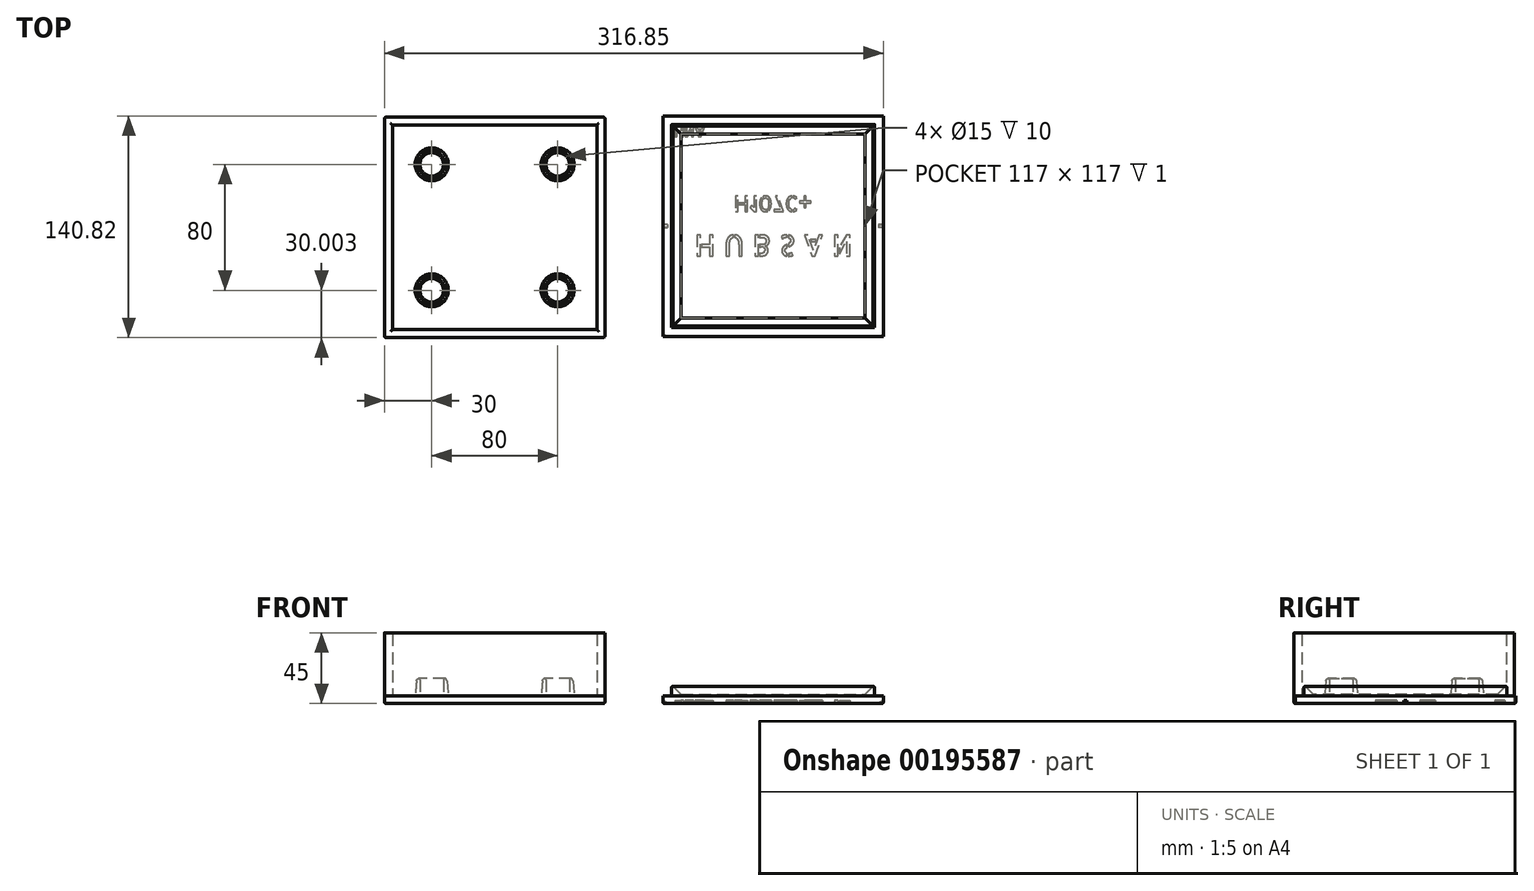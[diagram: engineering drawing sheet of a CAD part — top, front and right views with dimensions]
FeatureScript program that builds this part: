
annotation { "Feature Type Name" : "Feature", "Feature Type Description" : "" }
export const myFeature = defineFeature(function(context is Context, id is Id, definition is map)
    precondition{}
    {
        {
            var Q0;
            Q0=qCreatedBy(makeId("Top.planeOp"),FACE);
            var sketch = newSketch(context, id + "F0", { "sketchPlane" : qUnion([Q0])});
            skLineSegment(sketch, "E0.bottom", {"start": v(65, -65.82) * mm, "end": v(-65, -65.82) * mm});
            skLineSegment(sketch, "E0.top", {"start": v(65, 64.18) * mm, "end": v(-65, 64.18) * mm});
            skLineSegment(sketch, "E0.left", {"start": v(65, -65.82) * mm, "end": v(65, 64.18) * mm});
            skLineSegment(sketch, "E0.right", {"start": v(-65, -65.82) * mm, "end": v(-65, 64.18) * mm});
            skPoint(sketch, "E0.middle", {"position": v(0, -0.82) * mm});
            skLineSegment(sketch, "E1.0", {"start": v(70, 69.18) * mm, "end": v(-70, 69.18) * mm});
            skLineSegment(sketch, "E1.1", {"start": v(70, -70.82) * mm, "end": v(70, 69.18) * mm});
            skLineSegment(sketch, "E1.2", {"start": v(70, -70.82) * mm, "end": v(-70, -70.82) * mm});
            skLineSegment(sketch, "E1.3", {"start": v(-70, -70.82) * mm, "end": v(-70, 69.18) * mm});
            skCircle(sketch, "E2", {"center": v(-40, 39.18) * mm, "radius": 7.5 * mm});
            skCircle(sketch, "E3.0", {"center": v(-40, 39.18) * mm, "radius": 10.5 * mm});
            skCircle(sketch, "E4", {"center": v(-40, -40.82) * mm, "radius": 7.5 * mm});
            skCircle(sketch, "E5.0", {"center": v(-40, -40.82) * mm, "radius": 10.5 * mm});
            skCircle(sketch, "E6", {"center": v(40, -40.82) * mm, "radius": 7.5 * mm});
            skCircle(sketch, "E7.0", {"center": v(40, -40.82) * mm, "radius": 10.5 * mm});
            skCircle(sketch, "E8", {"center": v(40, 39.18) * mm, "radius": 7.5 * mm});
            skCircle(sketch, "E9.0", {"center": v(40, 39.18) * mm, "radius": 10.5 * mm});
            skSolve(sketch);
        }
        {
            var Q0;
            Q0=makeQuery(id+"F0.imprint","IMPRINT",FACE,{"disambiguationData":[TD([[makeQuery(id+"F0.imprint","IMPRINT",EDGE,{"derivedFrom":sQuery(id+"F0.wireOp",EDGE,"E2")}),-1.0]])]});
            var Q1;
            Q1=makeQuery(id+"F0.imprint","IMPRINT",FACE,{"disambiguationData":[TD([[makeQuery(id+"F0.imprint","IMPRINT",EDGE,{"derivedFrom":sQuery(id+"F0.wireOp",EDGE,"E8")}),-1.0]])]});
            var Q2;
            Q2=makeQuery(id+"F0.imprint","IMPRINT",FACE,{"disambiguationData":[TD([[makeQuery(id+"F0.imprint","IMPRINT",EDGE,{"derivedFrom":sQuery(id+"F0.wireOp",EDGE,"E6")}),-1.0]])]});
            var Q3;
            Q3=makeQuery(id+"F0.imprint","IMPRINT",FACE,{"disambiguationData":[TD([[makeQuery(id+"F0.imprint","IMPRINT",EDGE,{"derivedFrom":sQuery(id+"F0.wireOp",EDGE,"E4")}),-1.0]])]});
            extrude(context, id + "F1", {"entities" : qUnion([Q0, Q1, Q2, Q3]), "depth" : 11 * mm});
        }
        {
            var Q0;
            Q0=makeQuery(id+"F1.opExtrude","CAP_EDGE",EDGE,{"disambiguationData":[OSD([sQuery(id+"F0.wireOp",EDGE,"E5.0")])],"isStart":false});
            var Q1;
            Q1=makeQuery(id+"F1.opExtrude","CAP_EDGE",EDGE,{"disambiguationData":[OSD([sQuery(id+"F0.wireOp",EDGE,"E3.0")])],"isStart":false});
            var Q2;
            Q2=makeQuery(id+"F1.opExtrude","CAP_EDGE",EDGE,{"disambiguationData":[OSD([sQuery(id+"F0.wireOp",EDGE,"E7.0")])],"isStart":false});
            var Q3;
            Q3=makeQuery(id+"F1.opExtrude","CAP_EDGE",EDGE,{"disambiguationData":[OSD([sQuery(id+"F0.wireOp",EDGE,"E9.0")])],"isStart":false});
            chamfer(context, id + "F2", {"entities" : qUnion([Q0, Q1, Q2, Q3]), "chamferType" : ChamferType.OFFSET_ANGLE, "width" : 1 * mm, "oppositeDirection" : false, "angle" : 85 * degree, "tangentPropagation" : true});
        }
        {
            var Q0;
            Q0=makeQuery(id+"F1.opExtrude","CAP_EDGE",EDGE,{"disambiguationData":[OSD([sQuery(id+"F0.wireOp",EDGE,"E2")])],"isStart":false});
            var Q1;
            Q1=makeQuery(id+"F1.opExtrude","CAP_EDGE",EDGE,{"disambiguationData":[OSD([sQuery(id+"F0.wireOp",EDGE,"E4")])],"isStart":false});
            var Q2;
            Q2=makeQuery(id+"F1.opExtrude","CAP_EDGE",EDGE,{"disambiguationData":[OSD([sQuery(id+"F0.wireOp",EDGE,"E6")])],"isStart":false});
            var Q3;
            Q3=makeQuery(id+"F1.opExtrude","CAP_EDGE",EDGE,{"disambiguationData":[OSD([sQuery(id+"F0.wireOp",EDGE,"E8")])],"isStart":false});
            fillet(context, id + "F3", {"entities" : qUnion([Q0, Q1, Q2, Q3]), "radius" : 1 * mm, "tangentPropagation" : true, "allowEdgeOverflow" : false});
        }
        {
            var Q0;
            {var subQ0=sQuery(id+"F0.wireOp",EDGE,"E3.0");Q0=makeQuery(id+"F2.opChamfer","BLEND_EDGE",EDGE,{"blendedFrom":[makeQuery(id+"F1.opExtrude","CAP_EDGE",EDGE,{"disambiguationData":[OSD([subQ0])],"isStart":false}),makeQuery(id+"F1.opExtrude","CAP_FACE",FACE,{"disambiguationData":[OSD([sQuery(id+"F0.wireOp",EDGE,"E2"),subQ0])],"isStart":false})],"blendedInto":[makeQuery(id+"F1.opExtrude","CAP_FACE",FACE,{"disambiguationData":[OSD([sQuery(id+"F0.wireOp",EDGE,"E2"),subQ0])],"isStart":false})]});}
            var Q1;
            {var subQ0=sQuery(id+"F0.wireOp",EDGE,"E5.0");Q1=makeQuery(id+"F2.opChamfer","BLEND_EDGE",EDGE,{"blendedFrom":[makeQuery(id+"F1.opExtrude","CAP_EDGE",EDGE,{"disambiguationData":[OSD([subQ0])],"isStart":false}),makeQuery(id+"F1.opExtrude","CAP_FACE",FACE,{"disambiguationData":[OSD([sQuery(id+"F0.wireOp",EDGE,"E4"),subQ0])],"isStart":false})],"blendedInto":[makeQuery(id+"F1.opExtrude","CAP_FACE",FACE,{"disambiguationData":[OSD([sQuery(id+"F0.wireOp",EDGE,"E4"),subQ0])],"isStart":false})]});}
            var Q2;
            {var subQ0=sQuery(id+"F0.wireOp",EDGE,"E7.0");Q2=makeQuery(id+"F2.opChamfer","BLEND_EDGE",EDGE,{"blendedFrom":[makeQuery(id+"F1.opExtrude","CAP_EDGE",EDGE,{"disambiguationData":[OSD([subQ0])],"isStart":false}),makeQuery(id+"F1.opExtrude","CAP_FACE",FACE,{"disambiguationData":[OSD([sQuery(id+"F0.wireOp",EDGE,"E6"),subQ0])],"isStart":false})],"blendedInto":[makeQuery(id+"F1.opExtrude","CAP_FACE",FACE,{"disambiguationData":[OSD([sQuery(id+"F0.wireOp",EDGE,"E6"),subQ0])],"isStart":false})]});}
            var Q3;
            {var subQ0=sQuery(id+"F0.wireOp",EDGE,"E9.0");Q3=makeQuery(id+"F2.opChamfer","BLEND_EDGE",EDGE,{"blendedFrom":[makeQuery(id+"F1.opExtrude","CAP_EDGE",EDGE,{"disambiguationData":[OSD([subQ0])],"isStart":false}),makeQuery(id+"F1.opExtrude","CAP_FACE",FACE,{"disambiguationData":[OSD([sQuery(id+"F0.wireOp",EDGE,"E8"),subQ0])],"isStart":false})],"blendedInto":[makeQuery(id+"F1.opExtrude","CAP_FACE",FACE,{"disambiguationData":[OSD([sQuery(id+"F0.wireOp",EDGE,"E8"),subQ0])],"isStart":false})]});}
            fillet(context, id + "F4", {"entities" : qUnion([Q0, Q1, Q2, Q3]), "radius" : 2 * mm, "tangentPropagation" : true, "allowEdgeOverflow" : false});
        }
        {
            var Q0;
            Q0=makeQuery(id+"F0.imprint","IMPRINT",FACE,{"disambiguationData":[TD([[makeQuery(id+"F0.imprint","IMPRINT",EDGE,{"derivedFrom":sQuery(id+"F0.wireOp",EDGE,"E0.bottom")}),1.0]])]});
            extrude(context, id + "F5", {"entities" : qUnion([Q0]), "depth" : 40 * mm});
        }
        {
            var Q0;
            Q0=makeQuery(id+"F0.imprint","IMPRINT",FACE,{"disambiguationData":[TD([[makeQuery(id+"F0.imprint","IMPRINT",EDGE,{"derivedFrom":sQuery(id+"F0.wireOp",EDGE,"E0.bottom")}),-1.0]])]});
            var Q1;
            Q1=makeQuery(id+"F0.imprint","IMPRINT",FACE,{"disambiguationData":[TD([[makeQuery(id+"F0.imprint","IMPRINT",EDGE,{"derivedFrom":sQuery(id+"F0.wireOp",EDGE,"E0.bottom")}),1.0]])]});
            var Q2;
            Q2=makeQuery(id+"F0.imprint","IMPRINT",FACE,{"disambiguationData":[TD([[makeQuery(id+"F0.imprint","IMPRINT",EDGE,{"derivedFrom":sQuery(id+"F0.wireOp",EDGE,"E4")}),1.0]])]});
            var Q3;
            Q3=makeQuery(id+"F0.imprint","IMPRINT",FACE,{"disambiguationData":[TD([[makeQuery(id+"F0.imprint","IMPRINT",EDGE,{"derivedFrom":sQuery(id+"F0.wireOp",EDGE,"E4")}),-1.0]])]});
            var Q4;
            Q4=makeQuery(id+"F0.imprint","IMPRINT",FACE,{"disambiguationData":[TD([[makeQuery(id+"F0.imprint","IMPRINT",EDGE,{"derivedFrom":sQuery(id+"F0.wireOp",EDGE,"E2")}),-1.0]])]});
            var Q5;
            Q5=makeQuery(id+"F0.imprint","IMPRINT",FACE,{"disambiguationData":[TD([[makeQuery(id+"F0.imprint","IMPRINT",EDGE,{"derivedFrom":sQuery(id+"F0.wireOp",EDGE,"E2")}),1.0]])]});
            var Q6;
            Q6=makeQuery(id+"F0.imprint","IMPRINT",FACE,{"disambiguationData":[TD([[makeQuery(id+"F0.imprint","IMPRINT",EDGE,{"derivedFrom":sQuery(id+"F0.wireOp",EDGE,"E6")}),-1.0]])]});
            var Q7;
            Q7=makeQuery(id+"F0.imprint","IMPRINT",FACE,{"disambiguationData":[TD([[makeQuery(id+"F0.imprint","IMPRINT",EDGE,{"derivedFrom":sQuery(id+"F0.wireOp",EDGE,"E6")}),1.0]])]});
            var Q8;
            Q8=makeQuery(id+"F0.imprint","IMPRINT",FACE,{"disambiguationData":[TD([[makeQuery(id+"F0.imprint","IMPRINT",EDGE,{"derivedFrom":sQuery(id+"F0.wireOp",EDGE,"E8")}),-1.0]])]});
            var Q9;
            Q9=makeQuery(id+"F0.imprint","IMPRINT",FACE,{"disambiguationData":[TD([[makeQuery(id+"F0.imprint","IMPRINT",EDGE,{"derivedFrom":sQuery(id+"F0.wireOp",EDGE,"E8")}),1.0]])]});
            extrude(context, id + "F6", {"entities" : qUnion([Q0, Q1, Q2, Q3, Q4, Q5, Q6, Q7, Q8, Q9]), "oppositeDirection" : true, "depth" : 5 * mm});
        }
        {
            var Q0;
            Q0=makeQuery(id+"F6.opExtrude","CAP_EDGE",EDGE,{"disambiguationData":[OSD([sQuery(id+"F0.wireOp",EDGE,"E1.2")])],"isStart":false});
            var Q1;
            Q1=makeQuery(id+"F6.opExtrude","CAP_EDGE",EDGE,{"disambiguationData":[OSD([sQuery(id+"F0.wireOp",EDGE,"E1.3")])],"isStart":false});
            var Q2;
            Q2=makeQuery(id+"F6.opExtrude","CAP_EDGE",EDGE,{"disambiguationData":[OSD([sQuery(id+"F0.wireOp",EDGE,"E1.1")])],"isStart":false});
            var Q3;
            Q3=makeQuery(id+"F6.opExtrude","CAP_EDGE",EDGE,{"disambiguationData":[OSD([sQuery(id+"F0.wireOp",EDGE,"E1.0")])],"isStart":false});
            var Q4;
            Q4=makeQuery(id+"F6.opExtrude","SWEPT_EDGE",EDGE,{"disambiguationData":[OSD([sQuery(id+"F0.wireOp",EDGE,"E1.2"),sQuery(id+"F0.wireOp",EDGE,"E1.3")])]});
            var Q5;
            Q5=makeQuery(id+"F5.opExtrude","SWEPT_EDGE",EDGE,{"disambiguationData":[OSD([sQuery(id+"F0.wireOp",EDGE,"E1.2"),sQuery(id+"F0.wireOp",EDGE,"E1.3")])]});
            var Q6;
            Q6=makeQuery(id+"F5.opExtrude","SWEPT_EDGE",EDGE,{"disambiguationData":[OSD([sQuery(id+"F0.wireOp",EDGE,"E1.1"),sQuery(id+"F0.wireOp",EDGE,"E1.2")])]});
            var Q7;
            Q7=makeQuery(id+"F6.opExtrude","SWEPT_EDGE",EDGE,{"disambiguationData":[OSD([sQuery(id+"F0.wireOp",EDGE,"E1.1"),sQuery(id+"F0.wireOp",EDGE,"E1.2")])]});
            var Q8;
            Q8=makeQuery(id+"F6.opExtrude","SWEPT_EDGE",EDGE,{"disambiguationData":[OSD([sQuery(id+"F0.wireOp",EDGE,"E1.0"),sQuery(id+"F0.wireOp",EDGE,"E1.1")])]});
            var Q9;
            Q9=makeQuery(id+"F5.opExtrude","SWEPT_EDGE",EDGE,{"disambiguationData":[OSD([sQuery(id+"F0.wireOp",EDGE,"E1.0"),sQuery(id+"F0.wireOp",EDGE,"E1.1")])]});
            var Q10;
            Q10=makeQuery(id+"F6.opExtrude","SWEPT_EDGE",EDGE,{"disambiguationData":[OSD([sQuery(id+"F0.wireOp",EDGE,"E1.0"),sQuery(id+"F0.wireOp",EDGE,"E1.3")])]});
            var Q11;
            Q11=makeQuery(id+"F5.opExtrude","SWEPT_EDGE",EDGE,{"disambiguationData":[OSD([sQuery(id+"F0.wireOp",EDGE,"E1.0"),sQuery(id+"F0.wireOp",EDGE,"E1.3")])]});
            var Q12;
            Q12=makeQuery(id+"F5.opExtrude","CAP_EDGE",EDGE,{"disambiguationData":[OSD([sQuery(id+"F0.wireOp",EDGE,"E0.right")])],"isStart":false});
            var Q13;
            Q13=makeQuery(id+"F5.opExtrude","CAP_EDGE",EDGE,{"disambiguationData":[OSD([sQuery(id+"F0.wireOp",EDGE,"E0.bottom")])],"isStart":false});
            var Q14;
            Q14=makeQuery(id+"F5.opExtrude","CAP_EDGE",EDGE,{"disambiguationData":[OSD([sQuery(id+"F0.wireOp",EDGE,"E0.left")])],"isStart":false});
            var Q15;
            Q15=makeQuery(id+"F5.opExtrude","CAP_EDGE",EDGE,{"disambiguationData":[OSD([sQuery(id+"F0.wireOp",EDGE,"E0.top")])],"isStart":false});
            fillet(context, id + "F7", {"entities" : qUnion([Q0, Q1, Q2, Q3, Q4, Q5, Q6, Q7, Q8, Q9, Q10, Q11, Q12, Q13, Q14, Q15]), "radius" : 1 * mm, "tangentPropagation" : true, "allowEdgeOverflow" : false});
        }
        {
            var Q0;
            Q0=qCreatedBy(makeId("Top.planeOp"),FACE);
            var sketch = newSketch(context, id + "F8", { "sketchPlane" : qUnion([Q0])});
            skLineSegment(sketch, "E10.bottom", {"start": v(241.35, -64.5) * mm, "end": v(112.35, -64.5) * mm});
            skLineSegment(sketch, "E10.top", {"start": v(241.35, 64.5) * mm, "end": v(112.35, 64.5) * mm});
            skLineSegment(sketch, "E10.left", {"start": v(241.35, -64.5) * mm, "end": v(241.35, 64.5) * mm});
            skLineSegment(sketch, "E10.right", {"start": v(112.35, -64.5) * mm, "end": v(112.35, 64.5) * mm});
            skPoint(sketch, "E10.middle", {"position": v(176.85, 0) * mm});
            skLineSegment(sketch, "E11.0", {"start": v(106.85, -70) * mm, "end": v(106.85, 70) * mm});
            skLineSegment(sketch, "E11.1", {"start": v(246.85, -70) * mm, "end": v(106.85, -70) * mm});
            skLineSegment(sketch, "E11.2", {"start": v(246.85, -70) * mm, "end": v(246.85, 70) * mm});
            skLineSegment(sketch, "E11.3", {"start": v(246.85, 70) * mm, "end": v(106.85, 70) * mm});
            skLineSegment(sketch, "E12.0", {"start": v(118.35, -58.5) * mm, "end": v(118.35, 58.5) * mm});
            skLineSegment(sketch, "E12.1", {"start": v(235.35, -58.5) * mm, "end": v(118.35, -58.5) * mm});
            skLineSegment(sketch, "E12.2", {"start": v(235.35, -58.5) * mm, "end": v(235.35, 58.5) * mm});
            skLineSegment(sketch, "E12.3", {"start": v(235.35, 58.5) * mm, "end": v(118.35, 58.5) * mm});
            skLineSegment(sketch, "E13", {"start": v(106.85, 0) * mm, "end": v(246.85, 0) * mm, "construction": true});
            skLineSegment(sketch, "E14", {"start": v(176.85, -70) * mm, "end": v(176.85, 70) * mm, "construction": true});
            skSolve(sketch);
        }
        {
            var Q0;
            Q0=makeQuery(id+"F8.imprint","IMPRINT",FACE,{"disambiguationData":[TD([[makeQuery(id+"F8.imprint","IMPRINT",EDGE,{"derivedFrom":sQuery(id+"F8.wireOp",EDGE,"E10.bottom")}),-1.0]])]});
            extrude(context, id + "F9", {"entities" : qUnion([Q0]), "depth" : 6 * mm});
        }
        {
            var Q0;
            Q0=makeQuery(id+"F9.opExtrude","CAP_EDGE",EDGE,{"disambiguationData":[OSD([sQuery(id+"F8.wireOp",EDGE,"E12.0")])],"isStart":false});
            var Q1;
            Q1=makeQuery(id+"F9.opExtrude","CAP_EDGE",EDGE,{"disambiguationData":[OSD([sQuery(id+"F8.wireOp",EDGE,"E12.3")])],"isStart":false});
            var Q2;
            Q2=makeQuery(id+"F9.opExtrude","CAP_EDGE",EDGE,{"disambiguationData":[OSD([sQuery(id+"F8.wireOp",EDGE,"E12.1")])],"isStart":false});
            var Q3;
            Q3=makeQuery(id+"F9.opExtrude","CAP_EDGE",EDGE,{"disambiguationData":[OSD([sQuery(id+"F8.wireOp",EDGE,"E12.2")])],"isStart":false});
            chamfer(context, id + "F10", {"entities" : qUnion([Q0, Q1, Q2, Q3]), "width" : 5 * mm, "tangentPropagation" : true});
        }
        {
            var Q0;
            Q0=makeQuery(id+"F8.imprint","IMPRINT",FACE,{"disambiguationData":[TD([[makeQuery(id+"F8.imprint","IMPRINT",EDGE,{"derivedFrom":sQuery(id+"F8.wireOp",EDGE,"E10.bottom")}),1.0]])]});
            var Q1;
            Q1=makeQuery(id+"F8.imprint","IMPRINT",FACE,{"disambiguationData":[TD([[makeQuery(id+"F8.imprint","IMPRINT",EDGE,{"derivedFrom":sQuery(id+"F8.wireOp",EDGE,"E10.bottom")}),-1.0]])]});
            var Q2;
            Q2=makeQuery(id+"F8.imprint","IMPRINT",FACE,{"disambiguationData":[TD([[makeQuery(id+"F8.imprint","IMPRINT",EDGE,{"derivedFrom":sQuery(id+"F8.wireOp",EDGE,"E12.0")}),-1.0]])]});
            extrude(context, id + "F11", {"entities" : qUnion([Q0, Q1, Q2]), "operationType" : NewBodyOperationType.ADD, "oppositeDirection" : true, "depth" : 5 * mm});
        }
        {
            var Q0;
            Q0=makeQuery(id+"F11.opExtrude","CAP_EDGE",EDGE,{"disambiguationData":[OSD([sQuery(id+"F8.wireOp",EDGE,"E11.1")])],"isStart":false});
            var Q1;
            Q1=makeQuery(id+"F11.opExtrude","CAP_EDGE",EDGE,{"disambiguationData":[OSD([sQuery(id+"F8.wireOp",EDGE,"E11.0")])],"isStart":false});
            var Q2;
            Q2=makeQuery(id+"F11.opExtrude","CAP_EDGE",EDGE,{"disambiguationData":[OSD([sQuery(id+"F8.wireOp",EDGE,"E11.2")])],"isStart":false});
            var Q3;
            Q3=makeQuery(id+"F11.opExtrude","CAP_EDGE",EDGE,{"disambiguationData":[OSD([sQuery(id+"F8.wireOp",EDGE,"E11.3")])],"isStart":false});
            var Q4;
            Q4=makeQuery(id+"F9.opExtrude","CAP_EDGE",EDGE,{"disambiguationData":[OSD([sQuery(id+"F8.wireOp",EDGE,"E10.left")])],"isStart":false});
            var Q5;
            Q5=makeQuery(id+"F9.opExtrude","CAP_EDGE",EDGE,{"disambiguationData":[OSD([sQuery(id+"F8.wireOp",EDGE,"E10.bottom")])],"isStart":false});
            var Q6;
            Q6=makeQuery(id+"F9.opExtrude","CAP_EDGE",EDGE,{"disambiguationData":[OSD([sQuery(id+"F8.wireOp",EDGE,"E10.top")])],"isStart":false});
            var Q7;
            Q7=makeQuery(id+"F9.opExtrude","CAP_EDGE",EDGE,{"disambiguationData":[OSD([sQuery(id+"F8.wireOp",EDGE,"E10.right")])],"isStart":false});
            fillet(context, id + "F12", {"entities" : qUnion([Q0, Q1, Q2, Q3, Q4, Q5, Q6, Q7]), "radius" : 1 * mm, "tangentPropagation" : true, "allowEdgeOverflow" : false});
        }
        {
            var Q0;
            Q0=makeQuery(id+"F11.opExtrude","CAP_FACE",FACE,{"disambiguationData":[OSD([sQuery(id+"F8.wireOp",EDGE,"E11.0"),sQuery(id+"F8.wireOp",EDGE,"E11.1"),sQuery(id+"F8.wireOp",EDGE,"E11.2"),sQuery(id+"F8.wireOp",EDGE,"E11.3")])],"isStart":false});
            var sketch = newSketch(context, id + "F13", { "sketchPlane" : qUnion([Q0])});
            skText(sketch, "E15", { "text": "H U B S A N", "fontName": "AllertaStencil-Regular.ttf"});
            skText(sketch, "E16", { "text": "H107C+", "fontName": "AllertaStencil-Regular.ttf"});
            skLineSegment(sketch, "E17", {"start": v(176.85, -69) * mm, "end": v(176.85, 69) * mm, "construction": true});
            skText(sketch, "E18", { "text": "HNA", "fontName": "Arimo-Bold.ttf"});
            skLineSegment(sketch, "E19", {"start": v(107.85, 0) * mm, "end": v(245.85, 0) * mm, "construction": true});
            skLineSegment(sketch, "E20.bottom", {"start": v(109.85, -1) * mm, "end": v(105.85, -1) * mm});
            skLineSegment(sketch, "E20.top", {"start": v(109.85, 1) * mm, "end": v(105.85, 1) * mm});
            skLineSegment(sketch, "E20.left", {"start": v(109.85, -1) * mm, "end": v(109.85, 1) * mm});
            skLineSegment(sketch, "E20.right", {"start": v(105.85, -1) * mm, "end": v(105.85, 1) * mm});
            skPoint(sketch, "E20.middle", {"position": v(107.85, 0) * mm});
            skLineSegment(sketch, "E21.bottom", {"start": v(247.87, -1.03) * mm, "end": v(243.87, -1.03) * mm});
            skLineSegment(sketch, "E21.top", {"start": v(247.87, 0.97) * mm, "end": v(243.87, 0.97) * mm});
            skLineSegment(sketch, "E21.left", {"start": v(247.87, -1.03) * mm, "end": v(247.87, 0.97) * mm});
            skLineSegment(sketch, "E21.right", {"start": v(243.87, -1.03) * mm, "end": v(243.87, 0.97) * mm});
            skPoint(sketch, "E21.middle", {"position": v(245.87, -0.03) * mm});
            const initialGuessF13  = {"E15": [0.12685, 0.00565, 1, 0, 0.01335], "E16": [0.15185, -0.01906, 1, 0, 0.0097], "E18": [0.11385, -0.063, 1, 0, 0.00652]};
            skSetInitialGuess(sketch, initialGuessF13);
            skSolve(sketch);
        }
        {
            var Q0;
            Q0=makeQuery(id+"F13.imprint","IMPRINT",FACE,{"disambiguationData":[TD([[makeQuery(id+"F13.imprint","IMPRINT",EDGE,{"derivedFrom":sQuery(id+"F13.wireOp",EDGE,"E15.sketch_text.stroke-140")}),-1.0]])]});
            var Q1;
            Q1=makeQuery(id+"F13.imprint","IMPRINT",FACE,{"disambiguationData":[TD([[makeQuery(id+"F13.imprint","IMPRINT",EDGE,{"derivedFrom":sQuery(id+"F13.wireOp",EDGE,"E15.sketch_text.stroke-147")}),-1.0]])]});
            var Q2;
            Q2=makeQuery(id+"F13.imprint","IMPRINT",FACE,{"disambiguationData":[TD([[makeQuery(id+"F13.imprint","IMPRINT",EDGE,{"derivedFrom":sQuery(id+"F13.wireOp",EDGE,"E15.sketch_text.stroke-129")}),-1.0]])]});
            var Q3;
            Q3=makeQuery(id+"F13.imprint","IMPRINT",FACE,{"disambiguationData":[TD([[makeQuery(id+"F13.imprint","IMPRINT",EDGE,{"derivedFrom":sQuery(id+"F13.wireOp",EDGE,"E15.sketch_text.stroke-136")}),-1.0]])]});
            var Q4;
            Q4=makeQuery(id+"F13.imprint","IMPRINT",FACE,{"disambiguationData":[TD([[makeQuery(id+"F13.imprint","IMPRINT",EDGE,{"derivedFrom":sQuery(id+"F13.wireOp",EDGE,"E15.sketch_text.stroke-116")}),-1.0]])]});
            var Q5;
            Q5=makeQuery(id+"F13.imprint","IMPRINT",FACE,{"disambiguationData":[TD([[makeQuery(id+"F13.imprint","IMPRINT",EDGE,{"derivedFrom":sQuery(id+"F13.wireOp",EDGE,"E15.sketch_text.stroke-90")}),-1.0]])]});
            var Q6;
            Q6=makeQuery(id+"F13.imprint","IMPRINT",FACE,{"disambiguationData":[TD([[makeQuery(id+"F13.imprint","IMPRINT",EDGE,{"derivedFrom":sQuery(id+"F13.wireOp",EDGE,"E15.sketch_text.stroke-79")}),-1.0]])]});
            var Q7;
            Q7=makeQuery(id+"F13.imprint","IMPRINT",FACE,{"disambiguationData":[TD([[makeQuery(id+"F13.imprint","IMPRINT",EDGE,{"derivedFrom":sQuery(id+"F13.wireOp",EDGE,"E15.sketch_text.stroke-104")}),-1.0]])]});
            var Q8;
            Q8=makeQuery(id+"F13.imprint","IMPRINT",FACE,{"disambiguationData":[TD([[makeQuery(id+"F13.imprint","IMPRINT",EDGE,{"derivedFrom":sQuery(id+"F13.wireOp",EDGE,"E15.sketch_text.stroke-36")}),-1.0]])]});
            var Q9;
            Q9=makeQuery(id+"F13.imprint","IMPRINT",FACE,{"disambiguationData":[TD([[makeQuery(id+"F13.imprint","IMPRINT",EDGE,{"derivedFrom":sQuery(id+"F13.wireOp",EDGE,"E15.sketch_text.stroke-75")}),-1.0]])]});
            var Q10;
            Q10=makeQuery(id+"F13.imprint","IMPRINT",FACE,{"disambiguationData":[TD([[makeQuery(id+"F13.imprint","IMPRINT",EDGE,{"derivedFrom":sQuery(id+"F13.wireOp",EDGE,"E15.sketch_text.stroke-24")}),-1.0]])]});
            var Q11;
            Q11=makeQuery(id+"F13.imprint","IMPRINT",FACE,{"disambiguationData":[TD([[makeQuery(id+"F13.imprint","IMPRINT",EDGE,{"derivedFrom":sQuery(id+"F13.wireOp",EDGE,"E15.sketch_text.stroke-12")}),-1.0]])]});
            var Q12;
            Q12=makeQuery(id+"F13.imprint","IMPRINT",FACE,{"disambiguationData":[TD([[makeQuery(id+"F13.imprint","IMPRINT",EDGE,{"derivedFrom":sQuery(id+"F13.wireOp",EDGE,"E15.sketch_text.stroke-0")}),-1.0]])]});
            var Q13;
            Q13=makeQuery(id+"F13.imprint","IMPRINT",FACE,{"disambiguationData":[TD([[makeQuery(id+"F13.imprint","IMPRINT",EDGE,{"derivedFrom":sQuery(id+"F13.wireOp",EDGE,"E15.sketch_text.stroke-8")}),-1.0]])]});
            var Q14;
            Q14=makeQuery(id+"F13.imprint","IMPRINT",FACE,{"disambiguationData":[TD([[makeQuery(id+"F13.imprint","IMPRINT",EDGE,{"derivedFrom":sQuery(id+"F13.wireOp",EDGE,"E16.sketch_text.stroke-8")}),-1.0]])]});
            var Q15;
            Q15=makeQuery(id+"F13.imprint","IMPRINT",FACE,{"disambiguationData":[TD([[makeQuery(id+"F13.imprint","IMPRINT",EDGE,{"derivedFrom":sQuery(id+"F13.wireOp",EDGE,"E16.sketch_text.stroke-0")}),-1.0]])]});
            var Q16;
            Q16=makeQuery(id+"F13.imprint","IMPRINT",FACE,{"disambiguationData":[TD([[makeQuery(id+"F13.imprint","IMPRINT",EDGE,{"derivedFrom":sQuery(id+"F13.wireOp",EDGE,"E16.sketch_text.stroke-12")}),-1.0]])]});
            var Q17;
            Q17=makeQuery(id+"F13.imprint","IMPRINT",FACE,{"disambiguationData":[TD([[makeQuery(id+"F13.imprint","IMPRINT",EDGE,{"derivedFrom":sQuery(id+"F13.wireOp",EDGE,"E16.sketch_text.stroke-19")}),-1.0]])]});
            var Q18;
            Q18=makeQuery(id+"F13.imprint","IMPRINT",FACE,{"disambiguationData":[TD([[makeQuery(id+"F13.imprint","IMPRINT",EDGE,{"derivedFrom":sQuery(id+"F13.wireOp",EDGE,"E16.sketch_text.stroke-35")}),-1.0]])]});
            var Q19;
            Q19=makeQuery(id+"F13.imprint","IMPRINT",FACE,{"disambiguationData":[TD([[makeQuery(id+"F13.imprint","IMPRINT",EDGE,{"derivedFrom":sQuery(id+"F13.wireOp",EDGE,"E16.sketch_text.stroke-52")}),-1.0]])]});
            var Q20;
            Q20=makeQuery(id+"F13.imprint","IMPRINT",FACE,{"disambiguationData":[TD([[makeQuery(id+"F13.imprint","IMPRINT",EDGE,{"derivedFrom":sQuery(id+"F13.wireOp",EDGE,"E16.sketch_text.stroke-69")}),-1.0]])]});
            var Q21;
            Q21=makeQuery(id+"F13.imprint","IMPRINT",FACE,{"disambiguationData":[TD([[makeQuery(id+"F13.imprint","IMPRINT",EDGE,{"derivedFrom":sQuery(id+"F13.wireOp",EDGE,"E16.sketch_text.stroke-58")}),-1.0]])]});
            var Q22;
            Q22=makeQuery(id+"F13.imprint","IMPRINT",FACE,{"disambiguationData":[TD([[makeQuery(id+"F13.imprint","IMPRINT",EDGE,{"derivedFrom":sQuery(id+"F13.wireOp",EDGE,"E16.sketch_text.stroke-63")}),-1.0]])]});
            var Q23;
            Q23=makeQuery(id+"F13.imprint","IMPRINT",FACE,{"disambiguationData":[TD([[makeQuery(id+"F13.imprint","IMPRINT",EDGE,{"derivedFrom":sQuery(id+"F13.wireOp",EDGE,"E16.sketch_text.stroke-87")}),-1.0]])]});
            var Q24;
            Q24=makeQuery(id+"F13.imprint","IMPRINT",FACE,{"disambiguationData":[TD([[makeQuery(id+"F13.imprint","IMPRINT",EDGE,{"derivedFrom":sQuery(id+"F13.wireOp",EDGE,"E18.sketch_text.stroke-24")}),-1.0]])]});
            var Q25;
            Q25=makeQuery(id+"F13.imprint","IMPRINT",FACE,{"disambiguationData":[TD([[makeQuery(id+"F13.imprint","IMPRINT",EDGE,{"derivedFrom":sQuery(id+"F13.wireOp",EDGE,"E18.sketch_text.stroke-12")}),-1.0]])]});
            var Q26;
            Q26=makeQuery(id+"F13.imprint","IMPRINT",FACE,{"disambiguationData":[TD([[makeQuery(id+"F13.imprint","IMPRINT",EDGE,{"derivedFrom":sQuery(id+"F13.wireOp",EDGE,"E18.sketch_text.stroke-0")}),-1.0]])]});
            extrude(context, id + "F14", {"entities" : qUnion([Q0, Q1, Q2, Q3, Q4, Q5, Q6, Q7, Q8, Q9, Q10, Q11, Q12, Q13, Q14, Q15, Q16, Q17, Q18, Q19, Q20, Q21, Q22, Q23, Q24, Q25, Q26]), "operationType" : NewBodyOperationType.REMOVE, "oppositeDirection" : true, "depth" : 2 * mm});
        }
        {
            var Q0;
            {var subQ0=sQuery(id+"F13.wireOp",EDGE,"E21.right");Q0=makeQuery(id+"F13.imprint","IMPRINT",FACE,{"disambiguationData":[TD([[makeQuery(id+"F13.imprint","IMPRINT",EDGE,{"derivedFrom":subQ0}),-1.0]])]});}
            var Q1;
            {var subQ0=sQuery(id+"F13.wireOp",EDGE,"E21.left");Q1=makeQuery(id+"F13.imprint","IMPRINT",FACE,{"disambiguationData":[TD([[makeQuery(id+"F13.imprint","IMPRINT",EDGE,{"derivedFrom":subQ0}),1.0]])]});}
            var Q2;
            {var subQ0=sQuery(id+"F13.wireOp",EDGE,"E20.right");Q2=makeQuery(id+"F13.imprint","IMPRINT",FACE,{"disambiguationData":[TD([[makeQuery(id+"F13.imprint","IMPRINT",EDGE,{"derivedFrom":subQ0}),-1.0]])]});}
            var Q3;
            {var subQ0=sQuery(id+"F13.wireOp",EDGE,"E20.left");Q3=makeQuery(id+"F13.imprint","IMPRINT",FACE,{"disambiguationData":[TD([[makeQuery(id+"F13.imprint","IMPRINT",EDGE,{"derivedFrom":subQ0}),1.0]])]});}
            extrude(context, id + "F15", {"entities" : qUnion([Q0, Q1, Q2, Q3]), "operationType" : NewBodyOperationType.REMOVE, "oppositeDirection" : true, "depth" : 2 * mm});
        }
        {
            var Q0;
            Q0=makeQuery(id+"F15.boolean.opBoolean","COPY",FACE,{"derivedFrom":makeQuery(id+"F15.opExtrude","SWEPT_FACE",FACE,{"disambiguationData":[OSD([sQuery(id+"F13.wireOp",EDGE,"E20.top")])]})});
            var sketch = newSketch(context, id + "F16", { "sketchPlane" : qUnion([Q0])});
            skLineSegment(sketch, "E22", {"start": v(-106.85, -3) * mm, "end": v(-109.85, -5) * mm});
            skSolve(sketch);
        }
        {
            var Q0;
            Q0=makeQuery(id+"F16.imprint","IMPRINT",FACE,{"disambiguationData":[TD([[makeQuery(id+"F16.imprint","IMPRINT",EDGE,{"derivedFrom":sQuery(id+"F16.wireOp",EDGE,"E22")}),-1.0]])]});
            extrude(context, id + "F17", {"entities" : qUnion([Q0]), "operationType" : NewBodyOperationType.ADD, "endBound" : BoundingType.UP_TO_NEXT, "depth" : 3 * mm});
        }
        {
            var Q0;
            Q0=makeQuery(id+"F15.boolean.opBoolean","COPY",FACE,{"derivedFrom":makeQuery(id+"F15.opExtrude","SWEPT_FACE",FACE,{"disambiguationData":[OSD([sQuery(id+"F13.wireOp",EDGE,"E21.top")])]})});
            var sketch = newSketch(context, id + "F18", { "sketchPlane" : qUnion([Q0])});
            skLineSegment(sketch, "E23", {"start": v(-246.85, -3) * mm, "end": v(-243.87, -5) * mm});
            skSolve(sketch);
        }
        {
            var Q0;
            Q0=makeQuery(id+"F18.imprint","IMPRINT",FACE,{"disambiguationData":[TD([[makeQuery(id+"F18.imprint","IMPRINT",EDGE,{"derivedFrom":sQuery(id+"F18.wireOp",EDGE,"E23")}),1.0]])]});
            extrude(context, id + "F19", {"entities" : qUnion([Q0]), "operationType" : NewBodyOperationType.ADD, "endBound" : BoundingType.UP_TO_NEXT, "depth" : 25 * mm});
        }
    });
